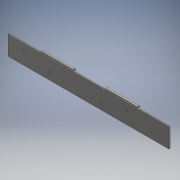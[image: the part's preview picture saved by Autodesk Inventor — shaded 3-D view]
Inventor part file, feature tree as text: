
AUTODESK INVENTOR PART (.ipt)
format: ipt  version: 2018 (Build 220112000, 112)  size: 175,104 bytes
history: native  units: mm
features: extrude x5, sketch x5, hole x1
ambient origin geometry x8: Origin, YZ Plane, XZ Plane, XY Plane, X Axis, Y Axis, Z Axis, Center Point
bodies: Solid1 (feature_tree)
feature tree (11):
  extrude  "Extrusion1"  Depth=30.0mm
  sketch  "Sketch2"  dims[d2=2.0mm d3=0.0mm d4=2.5mm]
  extrude  "Extrusion2"  Depth=2.0mm
  extrude  "Extrusion3"  Depth=3.5mm
  extrude  "Extrusion4"  Depth=250.0mm TaperAngle=0.0deg
  extrude  "Extrusion5"  Depth=2.0mm
  hole  "Hole1"  [1 undecoded]
  sketch  "Sketch1"  dims[d0=250.0mm d1=30.0mm]
  sketch  "Sketch3"  dims[d5=3.0mm d6=3.5mm]
  sketch  "Sketch4"  dims[d7=250.0mm d8=0.0mm d9=250.0mm d10=0.0mm]
  sketch  "Sketch5"  dims[d11=50.0mm d12=2.75mm d13=50.0mm d14=2.75mm d15=50.0mm d16=50.0mm d17=2.75mm d18=50.0mm d19=250.0mm d20=0.0mm d21=250.0mm d22=0.0mm d23=40.0mm d24=5.0mm d25=40.0mm d26=40.0mm d27=40.0mm d28=40.0mm d29=10.0mm d30=10.0mm d31=3.0mm d32=6.0mm d33=5.0mm d34=2.0mm d35=90.0deg d36=8.0mm d37=20.594885mm]
note: 1 required parameter value undecoded (feature->parameter linkage not recoverable at this tier; creation-order binding heuristic only, values carry confidence <= 0.55)
